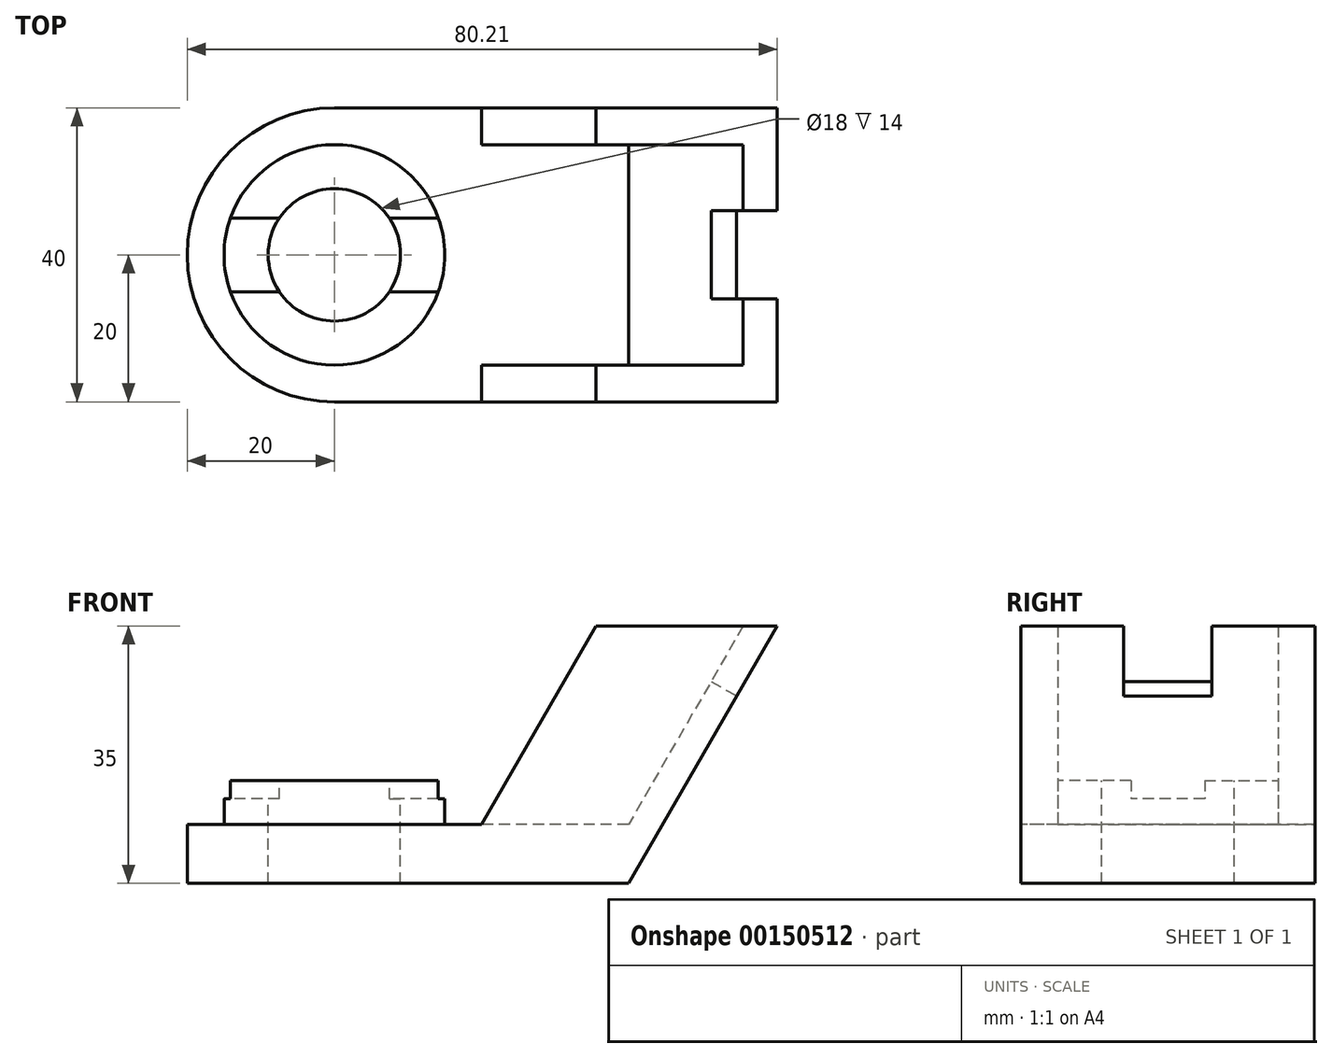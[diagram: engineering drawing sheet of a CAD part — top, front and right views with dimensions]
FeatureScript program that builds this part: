
annotation { "Feature Type Name" : "Feature", "Feature Type Description" : "" }
export const myFeature = defineFeature(function(context is Context, id is Id, definition is map)
    precondition{}
    {
        {
            var Q0;
            Q0=qCreatedBy(makeId("Front.planeOp"),FACE);
            var sketch = newSketch(context, id + "F0", { "sketchPlane" : qUnion([Q0])});
            skLineSegment(sketch, "E0.bottom", {"start": v(0, -8) * mm, "end": v(-40, -8) * mm});
            skLineSegment(sketch, "E0.top", {"start": v(0, 0) * mm, "end": v(-40, 0) * mm});
            skLineSegment(sketch, "E0.right", {"start": v(-40, -8) * mm, "end": v(-40, 0) * mm});
            skPoint(sketch, "E0.middle", {"position": v(0, 0) * mm});
            skLineSegment(sketch, "E1", {"start": v(0, -8) * mm, "end": v(0, 0) * mm});
            skSolve(sketch);
        }
        {
            var Q0;
            Q0 = qSketchRegion(id + "F0", true);
            extrude(context, id + "F1", {"entities" : qUnion([Q0]), "depth" : 40 * mm});
        }
        {
            var Q0;
            Q0=makeQuery(id+"F1.opExtrude","SWEPT_FACE",FACE,{"disambiguationData":[OSD([sQuery(id+"F0.wireOp",EDGE,"E0.top")])]});
            var sketch = newSketch(context, id + "F2", { "sketchPlane" : qUnion([Q0])});
            skPoint(sketch, "E2", {"position": v(-40, -20) * mm});
            skArc(sketch, "E3", {"start": v(-40, 0) * mm, "mid": v(-60, -20) * mm, "end": v(-40, -40) * mm});
            skSolve(sketch);
        }
        {
            var Q0;
            Q0=makeQuery(id+"F2.imprint","IMPRINT",FACE,{"disambiguationData":[TD([[makeQuery(id+"F2.imprint","IMPRINT",EDGE,{"derivedFrom":sQuery(id+"F2.wireOp",EDGE,"E3")}),1.0]])]});
            extrude(context, id + "F3", {"entities" : qUnion([Q0]), "operationType" : NewBodyOperationType.ADD, "oppositeDirection" : true, "depth" : 8 * mm});
        }
        {
            var Q0;
            {var subQ0=sQuery(id+"F0.wireOp",EDGE,"E0.top");Q0=makeQuery(id+"F3.boolean.opBoolean","MERGE",FACE,{"derivedFrom":[makeQuery(id+"F1.opExtrude","SWEPT_FACE",FACE,{"disambiguationData":[OSD([subQ0])]}),makeQuery(id+"F3.opExtrude","CAP_FACE",FACE,{"disambiguationData":[OSD([subQ0,sQuery(id+"F0.wireOp",EDGE,"E0.right"),sQuery(id+"F2.wireOp",EDGE,"E3")])],"isStart":true})]});}
            var sketch = newSketch(context, id + "F4", { "sketchPlane" : qUnion([Q0])});
            skCircle(sketch, "E4", {"center": v(-40, -20) * mm, "radius": 15 * mm});
            skSolve(sketch);
        }
        {
            var Q0;
            Q0=makeQuery(id+"F4.imprint","IMPRINT",FACE,{"disambiguationData":[TD([[makeQuery(id+"F4.imprint","IMPRINT",EDGE,{"derivedFrom":sQuery(id+"F4.wireOp",EDGE,"E4")}),1.0]])]});
            extrude(context, id + "F5", {"entities" : qUnion([Q0]), "operationType" : NewBodyOperationType.ADD, "depth" : 6 * mm});
        }
        {
            var Q0;
            Q0=makeQuery(id+"F5.opExtrude","CAP_FACE",FACE,{"disambiguationData":[OSD([sQuery(id+"F4.wireOp",EDGE,"E4")])],"isStart":false});
            var sketch = newSketch(context, id + "F6", { "sketchPlane" : qUnion([Q0])});
            skCircle(sketch, "E5", {"center": v(-40, -20) * mm, "radius": 9 * mm});
            skSolve(sketch);
        }
        {
            var Q0;
            Q0=makeQuery(id+"F6.imprint","IMPRINT",FACE,{"disambiguationData":[TD([[makeQuery(id+"F6.imprint","IMPRINT",EDGE,{"derivedFrom":sQuery(id+"F6.wireOp",EDGE,"E5")}),1.0]])]});
            extrude(context, id + "F7", {"entities" : qUnion([Q0]), "operationType" : NewBodyOperationType.REMOVE, "endBound" : BoundingType.THROUGH_ALL, "oppositeDirection" : true, "depth" : 25 * mm});
        }
        {
            var Q0;
            Q0=makeQuery(id+"F5.opExtrude","CAP_FACE",FACE,{"disambiguationData":[OSD([sQuery(id+"F4.wireOp",EDGE,"E4")])],"isStart":false});
            var sketch = newSketch(context, id + "F8", { "sketchPlane" : qUnion([Q0])});
            skLineSegment(sketch, "E6.bottom", {"start": v(-23.12, -25) * mm, "end": v(-56.88, -25) * mm});
            skLineSegment(sketch, "E6.top", {"start": v(-23.12, -15) * mm, "end": v(-56.88, -15) * mm});
            skLineSegment(sketch, "E6.left", {"start": v(-23.12, -25) * mm, "end": v(-23.12, -15) * mm});
            skLineSegment(sketch, "E6.right", {"start": v(-56.88, -25) * mm, "end": v(-56.88, -15) * mm});
            skPoint(sketch, "E6.middle", {"position": v(-40, -20) * mm});
            skSolve(sketch);
        }
        {
            var Q0;
            Q0 = qSketchRegion(id + "F8", true);
            extrude(context, id + "F9", {"entities" : qUnion([Q0]), "operationType" : NewBodyOperationType.REMOVE, "oppositeDirection" : true, "depth" : 2.5 * mm});
        }
        {
            var Q0;
            Q0=makeQuery(id+"F1.opExtrude","CAP_FACE",FACE,{"disambiguationData":[OSD([sQuery(id+"F0.wireOp",EDGE,"E0.bottom"),sQuery(id+"F0.wireOp",EDGE,"E0.top"),sQuery(id+"F0.wireOp",EDGE,"E0.right"),sQuery(id+"F0.wireOp",EDGE,"E1")])],"isStart":false});
            var sketch = newSketch(context, id + "F10", { "sketchPlane" : qUnion([Q0])});
            skLineSegment(sketch, "E7", {"start": v(0, -8) * mm, "end": v(20.2, 27) * mm});
            skLineSegment(sketch, "E8", {"start": v(20.2, 27) * mm, "end": v(15.59, 27) * mm});
            skLineSegment(sketch, "E9", {"start": v(15.59, 27) * mm, "end": v(0, 0) * mm});
            skSolve(sketch);
        }
        {
            var Q0;
            Q0 = qSketchRegion(id + "F10", true);
            var Q1;
            Q1=makeQuery(id+"F10.imprint","IMPRINT",FACE,{"disambiguationData":[TD([[makeQuery(id+"F10.imprint","IMPRINT",EDGE,{"derivedFrom":sQuery(id+"F10.wireOp",EDGE,"E7")}),1.0]])]});
            extrude(context, id + "F11", {"entities" : qUnion([Q0, Q1]), "operationType" : NewBodyOperationType.ADD, "oppositeDirection" : true, "depth" : 40 * mm});
        }
        {
            var Q0;
            {var subQ0=sQuery(id+"F0.wireOp",EDGE,"E1");Q0=makeQuery(id+"F11.boolean.opBoolean","MERGE",FACE,{"derivedFrom":[makeQuery(id+"F1.opExtrude","CAP_FACE",FACE,{"disambiguationData":[OSD([sQuery(id+"F0.wireOp",EDGE,"E0.bottom"),sQuery(id+"F0.wireOp",EDGE,"E0.top"),sQuery(id+"F0.wireOp",EDGE,"E0.right"),subQ0])],"isStart":false}),makeQuery(id+"F11.opExtrude","CAP_FACE",FACE,{"disambiguationData":[OSD([subQ0,sQuery(id+"F10.wireOp",EDGE,"E7"),sQuery(id+"F10.wireOp",EDGE,"E8"),sQuery(id+"F10.wireOp",EDGE,"E9")])],"isStart":true})]});}
            var sketch = newSketch(context, id + "F12", { "sketchPlane" : qUnion([Q0])});
            skLineSegment(sketch, "E10", {"start": v(-20, 0) * mm, "end": v(-4.41, 27) * mm});
            skLineSegment(sketch, "E11", {"start": v(-4.41, 27) * mm, "end": v(15.59, 27) * mm});
            skSolve(sketch);
        }
        {
            var Q0;
            {var subQ0=sQuery(id+"F12.wireOp",EDGE,"E10");Q0=makeQuery(id+"F12.imprint","IMPRINT",FACE,{"disambiguationData":[TD([[makeQuery(id+"F12.imprint","IMPRINT",EDGE,{"derivedFrom":subQ0}),-1.0]])]});}
            extrude(context, id + "F13", {"entities" : qUnion([Q0]), "operationType" : NewBodyOperationType.ADD, "oppositeDirection" : true, "depth" : 5 * mm});
        }
        {
            var Q0;
            {var subQ0=sQuery(id+"F0.wireOp",EDGE,"E1");Q0=makeQuery(id+"F11.boolean.opBoolean","MERGE",FACE,{"derivedFrom":[makeQuery(id+"F1.opExtrude","CAP_FACE",FACE,{"disambiguationData":[OSD([sQuery(id+"F0.wireOp",EDGE,"E0.bottom"),sQuery(id+"F0.wireOp",EDGE,"E0.top"),sQuery(id+"F0.wireOp",EDGE,"E0.right"),subQ0])],"isStart":true}),makeQuery(id+"F11.opExtrude","CAP_FACE",FACE,{"disambiguationData":[OSD([subQ0,sQuery(id+"F10.wireOp",EDGE,"E7"),sQuery(id+"F10.wireOp",EDGE,"E8"),sQuery(id+"F10.wireOp",EDGE,"E9")])],"isStart":false})]});}
            var sketch = newSketch(context, id + "F14", { "sketchPlane" : qUnion([Q0])});
            skLineSegment(sketch, "E12", {"start": v(20, 0) * mm, "end": v(4.41, 27) * mm});
            skLineSegment(sketch, "E13", {"start": v(4.41, 27) * mm, "end": v(-15.59, 27) * mm});
            skSolve(sketch);
        }
        {
            var Q0;
            Q0 = qSketchRegion(id + "F14", true);
            var Q1;
            {var subQ0=sQuery(id+"F14.wireOp",EDGE,"E12");Q1=makeQuery(id+"F14.imprint","IMPRINT",FACE,{"disambiguationData":[TD([[makeQuery(id+"F14.imprint","IMPRINT",EDGE,{"derivedFrom":subQ0}),1.0]])]});}
            extrude(context, id + "F15", {"entities" : qUnion([Q0, Q1]), "operationType" : NewBodyOperationType.ADD, "oppositeDirection" : true, "depth" : 5 * mm});
        }
        {
            var Q0;
            Q0=makeQuery(id+"F11.opExtrude","SWEPT_FACE",FACE,{"disambiguationData":[OSD([sQuery(id+"F10.wireOp",EDGE,"E7")])]});
            var sketch = newSketch(context, id + "F16", { "sketchPlane" : qUnion([Q0])});
            skLineSegment(sketch, "E14.bottom", {"start": v(-14, 22.49) * mm, "end": v(-26, 22.49) * mm});
            skLineSegment(sketch, "E14.top", {"start": v(-14, 33.49) * mm, "end": v(-26, 33.49) * mm});
            skLineSegment(sketch, "E14.left", {"start": v(-14, 22.49) * mm, "end": v(-14, 33.49) * mm});
            skLineSegment(sketch, "E14.right", {"start": v(-26, 22.49) * mm, "end": v(-26, 33.49) * mm});
            skPoint(sketch, "E14.middle", {"position": v(-20, 27.99) * mm});
            skPoint(sketch, "E14.middle.positionSnap0", {"position": v(-20, 33.49) * mm});
            skPoint(sketch, "E14.centerSnap0", {"position": v(-20, 33.49) * mm});
            skSolve(sketch);
        }
        {
            var Q0;
            Q0 = qSketchRegion(id + "F16", true);
            extrude(context, id + "F17", {"entities" : qUnion([Q0]), "operationType" : NewBodyOperationType.REMOVE, "oppositeDirection" : true, "depth" : 5 * mm});
        }
    });
